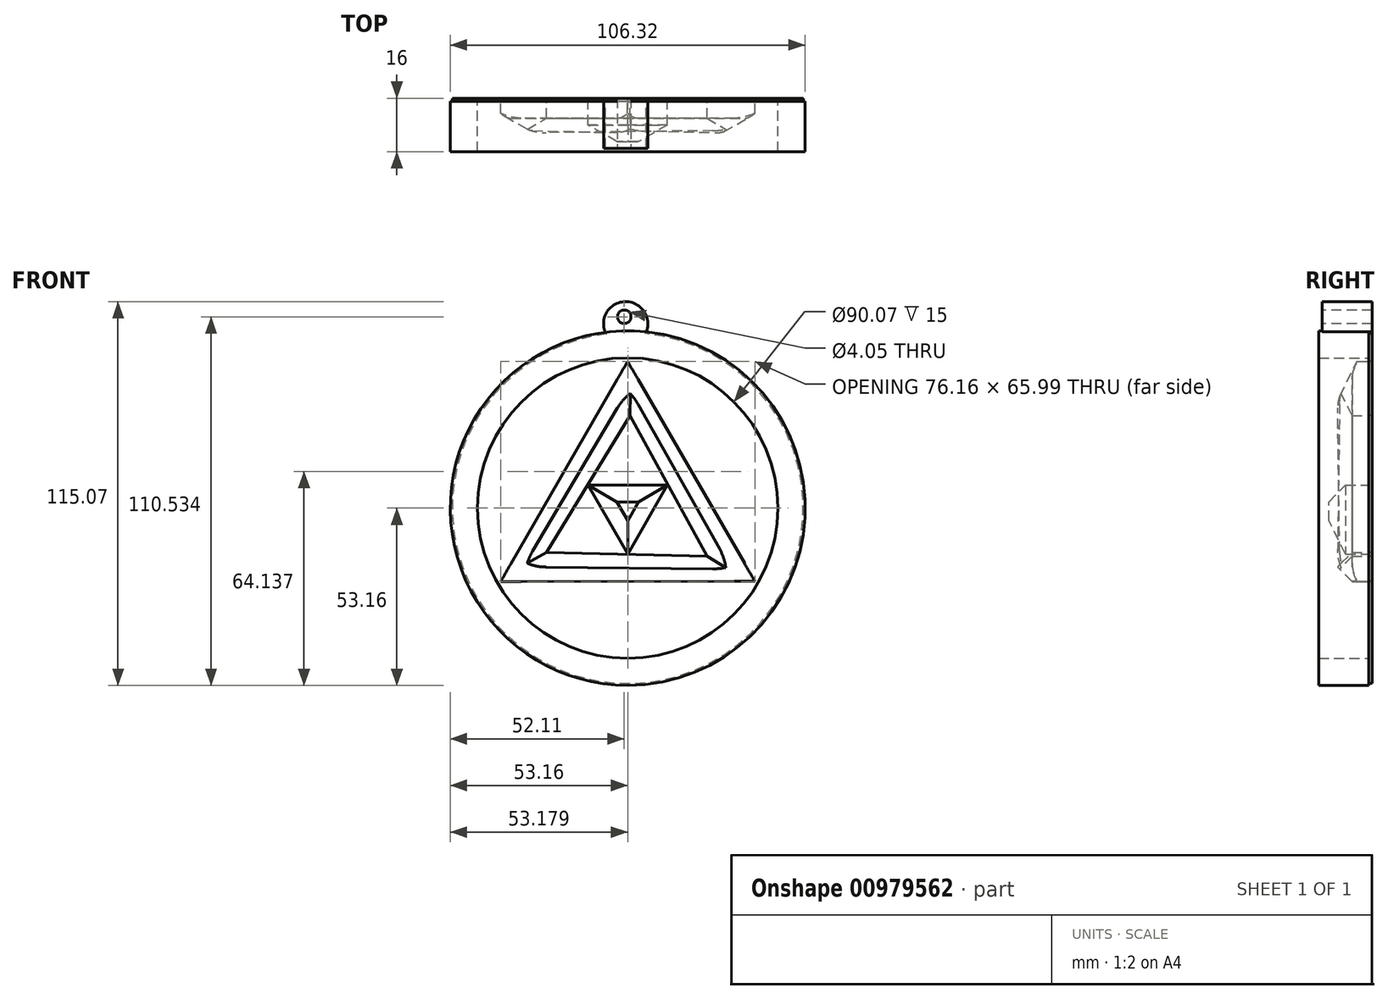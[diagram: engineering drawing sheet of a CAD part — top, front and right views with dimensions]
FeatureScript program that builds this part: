
annotation { "Feature Type Name" : "Feature", "Feature Type Description" : "" }
export const myFeature = defineFeature(function(context is Context, id is Id, definition is map)
    precondition{}
    {
        {
            var Q0;
            Q0=qCreatedBy(makeId("Front.planeOp"),FACE);
            var sketch = newSketch(context, id + "F0", { "sketchPlane" : qUnion([Q0])});
            skCircle(sketch, "E0", {"center": v(0, 0) * mm, "radius": 52.58 * mm});
            skSolve(sketch);
        }
        {
            var Q0;
            Q0 = qSketchRegion(id + "F0", true);
            extrude(context, id + "F1", {"entities" : qUnion([Q0]), "depth" : 1 * mm, "offsetDistance" : 25 * mm});
        }
        {
            var Q0;
            Q0=makeQuery(id+"F1.opExtrude","CAP_FACE",FACE,{"disambiguationData":[OSD([sQuery(id+"F0.wireOp",EDGE,"E0")])],"isStart":false});
            var sketch = newSketch(context, id + "F2", { "sketchPlane" : qUnion([Q0])});
            skCircle(sketch, "E1", {"center": v(0, 0) * mm, "radius": 53.16 * mm});
            skCircle(sketch, "E2", {"center": v(0, 0) * mm, "radius": 45.04 * mm});
            skSolve(sketch);
        }
        {
            var Q0;
            Q0 = qSketchRegion(id + "F2", true);
            extrude(context, id + "F3", {"entities" : qUnion([Q0]), "operationType" : NewBodyOperationType.ADD, "depth" : 15 * mm, "offsetDistance" : 25 * mm});
        }
        {
            var Q0;
            Q0=makeQuery(id+"F2.imprint","IMPRINT",FACE,{"disambiguationData":[TD([[makeQuery(id+"F2.imprint","IMPRINT",EDGE,{"derivedFrom":sQuery(id+"F2.wireOp",EDGE,"E2")}),1.0]])]});
            var sketch = newSketch(context, id + "F4", { "sketchPlane" : qUnion([Q0])});
            skCircle(sketch, "E3.cCircle", {"center": v(0, 0) * mm, "radius": 21.99 * mm, "construction": true});
            skLineSegment(sketch, "E3.0", {"start": v(38.1, -21.95) * mm, "end": v(-38.06, -22.02) * mm});
            skLineSegment(sketch, "E3.1", {"start": v(-38.06, -22.02) * mm, "end": v(-0.04, 43.97) * mm});
            skLineSegment(sketch, "E3.2", {"start": v(-0.04, 43.97) * mm, "end": v(38.1, -21.95) * mm});
            skPoint(sketch, "E3.0.midPoint", {"position": v(0.02, -21.99) * mm});
            skCircle(sketch, "E4.cCircle", {"center": v(0, 0) * mm, "radius": 13.9 * mm, "construction": true});
            skLineSegment(sketch, "E4.0", {"start": v(23.75, -14.43) * mm, "end": v(-24.37, -13.35) * mm});
            skLineSegment(sketch, "E4.1", {"start": v(-24.37, -13.35) * mm, "end": v(0.62, 27.78) * mm});
            skLineSegment(sketch, "E4.2", {"start": v(0.62, 27.78) * mm, "end": v(23.75, -14.43) * mm});
            skPoint(sketch, "E4.0.midPoint", {"position": v(-0.31, -13.9) * mm});
            skSolve(sketch);
        }
        {
            var Q0;
            Q0 = qSketchRegion(id + "F4", true);
            extrude(context, id + "F5", {"entities" : qUnion([Q0]), "operationType" : NewBodyOperationType.ADD, "depth" : 10 * mm, "offsetDistance" : 25 * mm});
        }
        {
            var Q0;
            Q0=makeQuery(id+"F4.imprint","IMPRINT",FACE,{"disambiguationData":[TD([[makeQuery(id+"F4.imprint","IMPRINT",EDGE,{"derivedFrom":sQuery(id+"F4.wireOp",EDGE,"E3.0")}),-1.0]])]});
            extrude(context, id + "F6", {"entities" : qUnion([Q0]), "operationType" : NewBodyOperationType.REMOVE, "oppositeDirection" : true, "depth" : 12 * mm, "offsetDistance" : 25 * mm});
        }
        {
            var Q0;
            Q0=makeQuery(id+"F4.imprint","IMPRINT",FACE,{"disambiguationData":[TD([[makeQuery(id+"F4.imprint","IMPRINT",EDGE,{"derivedFrom":sQuery(id+"F4.wireOp",EDGE,"E4.0")}),-1.0]])]});
            var sketch = newSketch(context, id + "F7", { "sketchPlane" : qUnion([Q0])});
            skCircle(sketch, "E5.cCircle", {"center": v(0, 0) * mm, "radius": 6.87 * mm, "construction": true});
            skLineSegment(sketch, "E5.0", {"start": v(11.9, 6.87) * mm, "end": v(0, -13.74) * mm});
            skLineSegment(sketch, "E5.1", {"start": v(0, -13.74) * mm, "end": v(-11.9, 6.87) * mm});
            skLineSegment(sketch, "E5.2", {"start": v(-11.9, 6.87) * mm, "end": v(11.9, 6.87) * mm});
            skPoint(sketch, "E5.0.midPoint", {"position": v(5.95, -3.43) * mm});
            skSolve(sketch);
        }
        {
            var Q0;
            Q0 = qSketchRegion(id + "F7", true);
            extrude(context, id + "F8", {"entities" : qUnion([Q0]), "operationType" : NewBodyOperationType.ADD, "depth" : 12 * mm, "offsetDistance" : 25 * mm});
        }
        {
            var Q0;
            Q0=makeQuery(id+"F8.opExtrude","CAP_EDGE",EDGE,{"disambiguationData":[OSD([sQuery(id+"F7.wireOp",EDGE,"E5.1")])],"isStart":false});
            var Q1;
            Q1=makeQuery(id+"F8.opExtrude","CAP_EDGE",EDGE,{"disambiguationData":[OSD([sQuery(id+"F7.wireOp",EDGE,"E5.0")])],"isStart":false});
            var Q2;
            Q2=makeQuery(id+"F8.opExtrude","CAP_EDGE",EDGE,{"disambiguationData":[OSD([sQuery(id+"F7.wireOp",EDGE,"E5.2")])],"isStart":false});
            chamfer(context, id + "F9", {"entities" : qUnion([Q0, Q1, Q2]), "width" : 5 * mm, "tangentPropagation" : true});
        }
        {
            var Q0;
            Q0=makeQuery(id+"F5.opExtrude","CAP_EDGE",EDGE,{"disambiguationData":[OSD([sQuery(id+"F4.wireOp",EDGE,"E4.1")])],"isStart":false});
            var Q1;
            Q1=makeQuery(id+"F5.opExtrude","CAP_EDGE",EDGE,{"disambiguationData":[OSD([sQuery(id+"F4.wireOp",EDGE,"E4.0")])],"isStart":false});
            var Q2;
            Q2=makeQuery(id+"F5.opExtrude","CAP_EDGE",EDGE,{"disambiguationData":[OSD([sQuery(id+"F4.wireOp",EDGE,"E4.2")])],"isStart":false});
            chamfer(context, id + "F10", {"entities" : qUnion([Q0, Q1, Q2]), "width" : 5 * mm, "tangentPropagation" : true});
        }
        {
            var Q0;
            Q0=makeQuery(id+"F5.opExtrude","CAP_EDGE",EDGE,{"disambiguationData":[OSD([sQuery(id+"F4.wireOp",EDGE,"E3.1")])],"isStart":false});
            var Q1;
            Q1=makeQuery(id+"F5.opExtrude","CAP_EDGE",EDGE,{"disambiguationData":[OSD([sQuery(id+"F4.wireOp",EDGE,"E3.0")])],"isStart":false});
            var Q2;
            Q2=makeQuery(id+"F5.opExtrude","CAP_EDGE",EDGE,{"disambiguationData":[OSD([sQuery(id+"F4.wireOp",EDGE,"E3.2")])],"isStart":false});
            chamfer(context, id + "F11", {"entities" : qUnion([Q0, Q1, Q2]), "width" : 5 * mm, "tangentPropagation" : true});
        }
        {
            var Q0;
            Q0=makeQuery(id+"F11.opChamfer","BLEND_EDGE",EDGE,{"blendedFrom":[makeQuery(id+"F5.opExtrude","CAP_EDGE",EDGE,{"disambiguationData":[OSD([sQuery(id+"F4.wireOp",EDGE,"E3.1")])],"isStart":false}),makeQuery(id+"F5.opExtrude","CAP_EDGE",EDGE,{"disambiguationData":[OSD([sQuery(id+"F4.wireOp",EDGE,"E3.2")])],"isStart":false})],"blendedInto":[]});
            fillet(context, id + "F12", {"entities" : qUnion([Q0]), "radius" : 5 * mm, "tangentPropagation" : true, "allowEdgeOverflow" : false});
        }
        {
            var Q0;
            Q0=makeQuery(id+"F11.opChamfer","BLEND_EDGE",EDGE,{"blendedFrom":[makeQuery(id+"F5.opExtrude","CAP_EDGE",EDGE,{"disambiguationData":[OSD([sQuery(id+"F4.wireOp",EDGE,"E3.0")])],"isStart":false}),makeQuery(id+"F5.opExtrude","CAP_EDGE",EDGE,{"disambiguationData":[OSD([sQuery(id+"F4.wireOp",EDGE,"E3.1")])],"isStart":false})],"blendedInto":[]});
            fillet(context, id + "F13", {"entities" : qUnion([Q0]), "radius" : 5 * mm, "tangentPropagation" : true, "allowEdgeOverflow" : false});
        }
        {
            var Q0;
            Q0=makeQuery(id+"F11.opChamfer","BLEND_EDGE",EDGE,{"blendedFrom":[makeQuery(id+"F5.opExtrude","CAP_EDGE",EDGE,{"disambiguationData":[OSD([sQuery(id+"F4.wireOp",EDGE,"E3.0")])],"isStart":false}),makeQuery(id+"F5.opExtrude","CAP_EDGE",EDGE,{"disambiguationData":[OSD([sQuery(id+"F4.wireOp",EDGE,"E3.2")])],"isStart":false})],"blendedInto":[]});
            fillet(context, id + "F14", {"entities" : qUnion([Q0]), "radius" : 5 * mm, "tangentPropagation" : true, "allowEdgeOverflow" : false});
        }
        {
            var Q0;
            Q0=qCreatedBy(makeId("Front.planeOp"),FACE);
            var sketch = newSketch(context, id + "F15", { "sketchPlane" : qUnion([Q0])});
            skArc(sketch, "E6", {"start": v(5.52, 52.83) * mm, "mid": v(-0.78, 61.91) * mm, "end": v(-6.66, 52.55) * mm});
            skArc(sketch, "E7", {"start": v(-6.66, 52.55) * mm, "mid": v(-0.5, 49.8) * mm, "end": v(5.52, 52.83) * mm});
            skSolve(sketch);
        }
        {
            var Q0;
            Q0 = qSketchRegion(id + "F15", true);
            extrude(context, id + "F16", {"entities" : qUnion([Q0]), "operationType" : NewBodyOperationType.ADD, "depth" : 15 * mm, "offsetDistance" : 25 * mm});
        }
        {
            var Q0;
            Q0=makeQuery(id+"F16.opExtrude","CAP_FACE",FACE,{"disambiguationData":[OSD([sQuery(id+"F15.wireOp",EDGE,"E6"),sQuery(id+"F15.wireOp",EDGE,"E7")])],"isStart":false});
            var sketch = newSketch(context, id + "F17", { "sketchPlane" : qUnion([Q0])});
            skCircle(sketch, "E8", {"center": v(-1.05, 57.37) * mm, "radius": 2.02 * mm});
            skSolve(sketch);
        }
        {
            var Q0;
            Q0=makeQuery(id+"F17.imprint","IMPRINT",FACE,{"disambiguationData":[TD([[makeQuery(id+"F17.imprint","IMPRINT",EDGE,{"derivedFrom":sQuery(id+"F17.wireOp",EDGE,"E8")}),1.0]])]});
            extrude(context, id + "F18", {"entities" : qUnion([Q0]), "operationType" : NewBodyOperationType.REMOVE, "oppositeDirection" : true, "depth" : 25 * mm, "offsetDistance" : 25 * mm});
        }
    });
